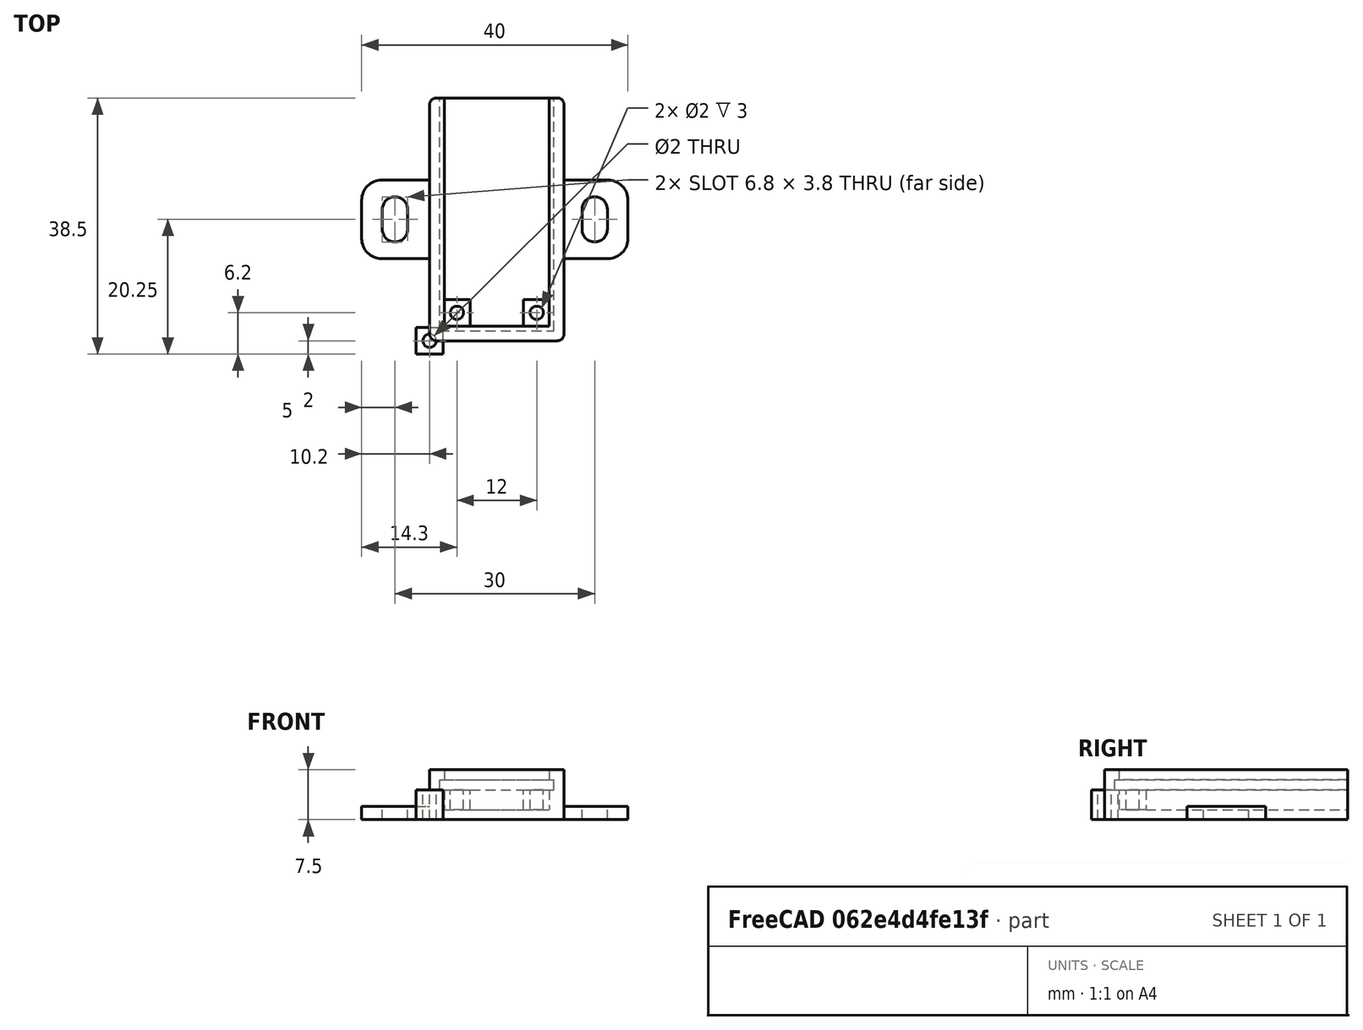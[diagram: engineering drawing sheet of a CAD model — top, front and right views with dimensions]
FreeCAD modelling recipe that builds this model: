
FCSTD DOCUMENT  (FreeCAD 0.19R23578 (Git))
Label: mosfet_d4184a
License: FreeArt
LicenseURL: http://artlibre.org/licence/lal
objects: Part::Box×4, Part::MultiFuse×3, Part::Cut×2, Spreadsheet::Sheet×1, Part::Fillet×1, Part::Feature×1, Part::Cylinder×1, Part::FeaturePython×1, App::Part×1
note: 12 computed .brp shape members not serialized (recipe doc carries the construction recipe); baked Part::Feature solids carry a one-line shape summary decoded from their .brp

FEATURE [Spreadsheet::Sheet] Spreadsheet  label="p"
  cells = A1=pcb_x; B1(pcb_x)=17.2; A2=pcb_y; B2(pcb_y)=35; A3=pcb_z; B3(pcb_z)=1.5; A4=pcb_under; B4(pcb_under)=3; A5=side_wall; B5(side_wall)=1.5; A6=pcb_side_lane; B6(pcb_side_lane)=0.7; A7=bottom_wall; B7(bottom_wall)=1.5; A8=pcb_above; B8(pcb_above)=1.5; A9=hole_dist_x; B9(hole_dist_x)=12; A10=hole_r; B10(hole_r)=1; A11=hole_off_y; B11(hole_off_y)=2; A12=hole_stand_size; B12(hole_stand_size)=4
FEATURE [Part::Box] Box  label="external cube"
  AttacherType = Attacher::AttachEngine3D
  Height = 7.5
  Length = 20.2
  Width = 36.5
  expr: Height = <<p>>.bottom_wall + <<p>>.pcb_under + <<p>>.pcb_z + <<p>>.pcb_above
  expr: Width = <<p>>.pcb_y + <<p>>.side_wall
  expr: Length = <<p>>.pcb_x + 2 * <<p>>.side_wall
FEATURE [Part::Box] Box006  label="internal cube"
  AttacherType = Attacher::AttachEngine3D
  Height = 6
  Length = 15.8
  Placement = pos=(2.2,2.2,1.5) rot=(0,0,1;0rad)
  Width = 35.1
  expr: .Placement.Base.y = <<p>>.side_wall + <<p>>.pcb_side_lane
  expr: .Placement.Base.x = <<p>>.side_wall + <<p>>.pcb_side_lane
  expr: .Placement.Base.z = <<p>>.bottom_wall
  expr: Height = <<p>>.pcb_under + <<p>>.pcb_z + <<p>>.pcb_above
  expr: Width = <<p>>.pcb_y - 2 * <<p>>.pcb_side_lane + <<p>>.side_wall
  expr: Length = <<p>>.pcb_x - 2 * <<p>>.pcb_side_lane
FEATURE [Part::Box] Box007  label="pcb extract cube"
  AttacherType = Attacher::AttachEngine3D
  Height = 1.5
  Length = 17.2
  Placement = pos=(1.5,1.5,4.5) rot=(0,0,1;0rad)
  Width = 35
  expr: .Placement.Base.y = <<p>>.side_wall
  expr: .Placement.Base.x = <<p>>.side_wall
  expr: Length = <<p>>.pcb_x
  expr: Width = <<p>>.pcb_y
  expr: .Placement.Base.z = <<p>>.bottom_wall + <<p>>.pcb_under
  expr: Height = <<p>>.pcb_z
FEATURE [Part::MultiFuse] Fusion  label="extract fusion"
  Shapes = -> [Box006,Box007]
FEATURE [Part::Fillet] Fillet  label="external fillet"
  Base = -> Box
  Edges = 4 edges r=1: [Edge1,Edge3,Edge5,Edge7]
FEATURE [Part::Feature] Cut003001  label="attach plane x dir001"
  Placement = pos=(-10.2,12.35,0) rot=(0,0,1;0rad)
  shape: bbox 40 x 11.8 x 2 mm, 18 faces (baked)
FEATURE [Part::MultiFuse] Fusion001  label="body fusion"
  Shapes = -> [Fillet,Cut003001]
FEATURE [Part::Cut] Cut  label="d4184a cut"
  Base = -> Fusion001
  Tool = -> Fusion
FEATURE [Part::Cylinder] Cylinder  label="hole"
  Angle = 360
  AttacherType = Attacher::AttachEngine3D
  Height = 10
  Radius = 1
  expr: Radius = <<p>>.hole_r
FEATURE [Part::Box] Box008  label="stand"
  AttacherType = Attacher::AttachEngine3D
  Height = 4.5
  Length = 4
  Placement = pos=(-2,-2,0) rot=(0,0,1;0rad)
  Width = 4
  expr: Height = <<p>>.pcb_under + <<p>>.bottom_wall
  expr: Length = <<p>>.hole_stand_size
  expr: Width = <<p>>.hole_stand_size
  expr: .Placement.Base.x = -<<p>>.hole_stand_size / 2
  expr: .Placement.Base.y = -<<p>>.hole_stand_size / 2
FEATURE [Part::Cut] Cut003002  label="stand hole cut"
  Base = -> Box008
  Tool = -> Cylinder
FEATURE [Part::FeaturePython] Array  label="hole array"  # Draft array (typed FeaturePython)
  Angle = 360
  ArrayType = 0
  Axis = (0,0,1)
  Base = -> Cut003002
  Center = (0,0,0)
  Count = 2
  ExpandArray = false
  Fuse = false
  IntervalAxis = (0,0,0)
  IntervalX = (12,0,0)
  IntervalY = (0,100,0)
  IntervalZ = (0,0,100)
  NumberCircles = 3
  NumberPolar = 5
  NumberX = 2
  NumberY = 1
  NumberZ = 1
  Placement = pos=(4.1,4.2,0) rot=(0,0,1;0rad)
  PlacementList = 2 placements: [(0,0,0),(12,0,0)]
  RadialDistance = 50
  ScaleList = (2) [(1,1,1),(1,1,1)]
  Symmetry = 1
  TangentialDistance = 25
  expr: .IntervalX.x = <<p>>.hole_dist_x
  expr: .Placement.Base.y = <<p>>.hole_off_y + <<p>>.side_wall + <<p>>.pcb_side_lane
  expr: .Placement.Base.x = (2 * <<p>>.side_wall + <<p>>.pcb_x - <<p>>.hole_dist_x) / 2
FEATURE [Part::MultiFuse] Fusion002  label="d4184a fusion"
  Shapes = -> [Array,Cut]
FEATURE [App::Part] Part  label="d4184a pcb box part"
  Group = -> [Box,Fillet,Fusion001,Fusion,Box007,Box006,Cut,Cylinder,Box008,Cut003001,Cut003002,Array,Fusion002]
  Origin = -> Origin
